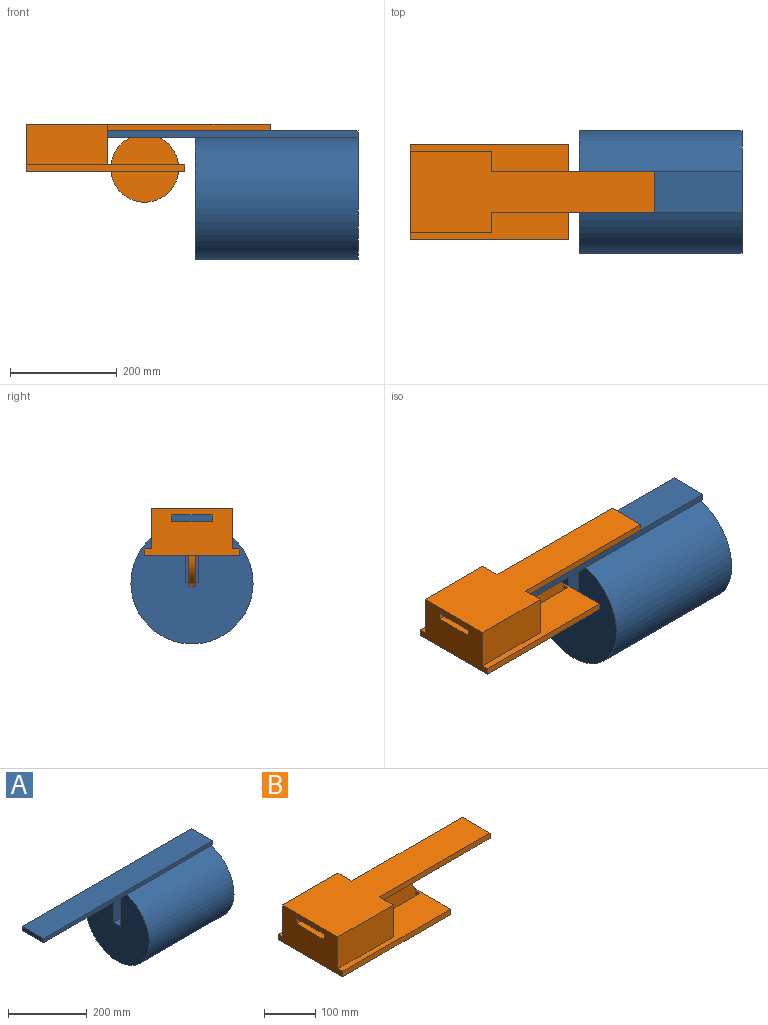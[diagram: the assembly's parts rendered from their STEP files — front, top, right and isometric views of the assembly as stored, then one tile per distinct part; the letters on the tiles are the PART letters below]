
ASSEMBLY  parts=2 mates=1
PART A: 19 faces, bbox 609.6x228.6x241.3 mm
  f0: plane 25.4x0.71mm, normal (0,-1,0), area 18mm2, adj f7,f8,f9,f14
  f1: plane 25.4x0.71mm, normal (0,1,0), area 18mm2, adj f7,f8,f9,f14
  f2: plane 609.6x12.7mm, normal (0,-1,0), area 7741.9mm2, adj f3,f5,f6,f7
  f3: plane 76.2x12.7mm, normal (1,0,0), area 967.7mm2, adj f2,f4,f6,f7
  f4: plane 609.6x12.7mm, normal (0,1,0), area 7741.9mm2, adj f3,f5,f6,f7
  f5: plane 76.2x12.7mm, normal (-1,0,0), area 967.7mm2, adj f2,f4,f6,f7
  f6: plane 609.6x76.2mm, normal (0,0,1), area 46451.5mm2, adj f2,f3,f4,f5
  f7: plane 609.6x76.2mm, normal (0,0,-1), area 45806.4mm2, adj f0,f1,f2,f3,f4,f5,f8,f9
  f8: plane 114.3x25.4mm, normal (1,0,0), area 2903.2mm2, adj f0,f1,f7,f10,f11,f12
  f9: plane 114.3x25.4mm, normal (-1,0,0), area 2903.2mm2, adj f0,f1,f7,f13,f15,f16
  f10: plane 152.4x113.59mm, normal (0,1,0), area 17311.5mm2, adj f8,f12,f14,f17
  f11: plane 152.4x113.59mm, normal (0,-1,0), area 17311.5mm2, adj f8,f12,f14,f17
  f12: plane 152.4x25.4mm, normal (0,0,1), area 3871mm2, adj f8,f10,f11,f17
  f13: plane 127x113.59mm, normal (0,1,0), area 14426.2mm2, adj f9,f14,f16,f18
  f14: cylinder r=114.3mm len=304.8mm, axis (-1,0,0), area 211139.7mm2, adj f0,f1,f10,f11,f13,f15,f17,f18
  f15: plane 127x113.59mm, normal (0,-1,0), area 14426.2mm2, adj f9,f14,f16,f18
  f16: plane 127x25.4mm, normal (0,0,1), area 3225.8mm2, adj f9,f13,f15,f18
  f17: plane 228.6x227.89mm, normal (1,0,0), area 38146.1mm2, adj f10,f11,f12,f14
  f18: plane 228.6x227.89mm, normal (-1,0,0), area 38146.1mm2, adj f13,f14,f15,f16
PART B: 25 faces, bbox 457.2x177.8x146.1 mm
  f0: plane 152.4x12.7mm, normal (0,1,0), area 1935.5mm2, adj f2,f4,f6,f23
  f1: plane 152.4x12.7mm, normal (0,-1,0), area 1935.5mm2, adj f2,f4,f6,f23
  f2: plane 152.4x76.2mm, normal (0,0,1), area 11612.9mm2, adj f0,f1,f4,f6
  f3: plane 152.4x76.2mm, normal (0,-1,0), area 11612.9mm2, adj f4,f6,f7,f20
  f4: plane 152.4x88.9mm, normal (1,0,0), area 9903.2mm2, adj f0,f1,f2,f3,f5,f7,f11,f12
  f5: plane 152.4x76.2mm, normal (0,1,0), area 11612.9mm2, adj f4,f6,f7,f20
  f6: plane 177.8x88.9mm, normal (-1,0,0), area 12903.2mm2, adj f0,f1,f2,f3,f5,f7,f8,f13
  f7: plane 297.18x177.8mm, normal (0,0,1), area 27129mm2, adj f3,f4,f5,f6,f8,f9,f10,f11
  f8: plane 297.18x12.7mm, normal (0,1,0), area 3774.2mm2, adj f6,f7,f9,f14
  f9: plane 177.8x12.7mm, normal (1,0,0), area 2258.1mm2, adj f7,f8,f13,f14
  f10: plane 17.78x12.7mm, normal (-1,0,0), area 225.8mm2, adj f7,f11,f12,f14
  f11: plane 139.7x12.7mm, normal (0,-1,0), area 1742.5mm2, adj f4,f7,f10,f14,f15
  f12: plane 139.7x12.7mm, normal (0,1,0), area 1742.5mm2, adj f4,f7,f10,f14,f16
  f13: plane 297.18x12.7mm, normal (0,-1,0), area 3774.2mm2, adj f6,f7,f9,f14
  f14: plane 297.18x177.8mm, normal (0,0,-1), area 50354.7mm2, adj f4,f6,f8,f9,f10,f11,f12,f13
  f15: cylinder r=3.17mm len=6.35mm, axis (0,1,0), area 50.7mm2, adj f11,f18
  f16: cylinder r=3.17mm len=6.35mm, axis (0,-1,0), area 50.7mm2, adj f12,f19
  f17: cylinder r=63.5mm len=127mm, axis (0,-1,0), area 5067.1mm2, adj f18,f19
  f18: plane 127x127mm, normal (0,1,0), area 12636mm2, adj f15,f17
  f19: plane 127x127mm, normal (0,-1,0), area 12636mm2, adj f16,f17
  f20: plane 457.2x152.4mm, normal (0,0,1), area 46451.5mm2, adj f3,f4,f5,f6,f21,f22,f24
  f21: plane 304.8x12.7mm, normal (0,-1,0), area 3871mm2, adj f4,f20,f23,f24
  f22: plane 304.8x12.7mm, normal (0,1,0), area 3871mm2, adj f4,f20,f23,f24
  f23: plane 457.2x76.2mm, normal (0,0,-1), area 34838.6mm2, adj f0,f1,f6,f21,f22,f24
  f24: plane 76.2x12.7mm, normal (1,0,0), area 967.7mm2, adj f20,f21,f22,f23
PLACE A t=(479.69,137.08,278.39)mm
PLACE B t=(239.36,137.08,227.59)mm
MATE slider B.f6 <-> A.f5  axis (-1,0,0) through (163.16,137.08,291.09)mm
